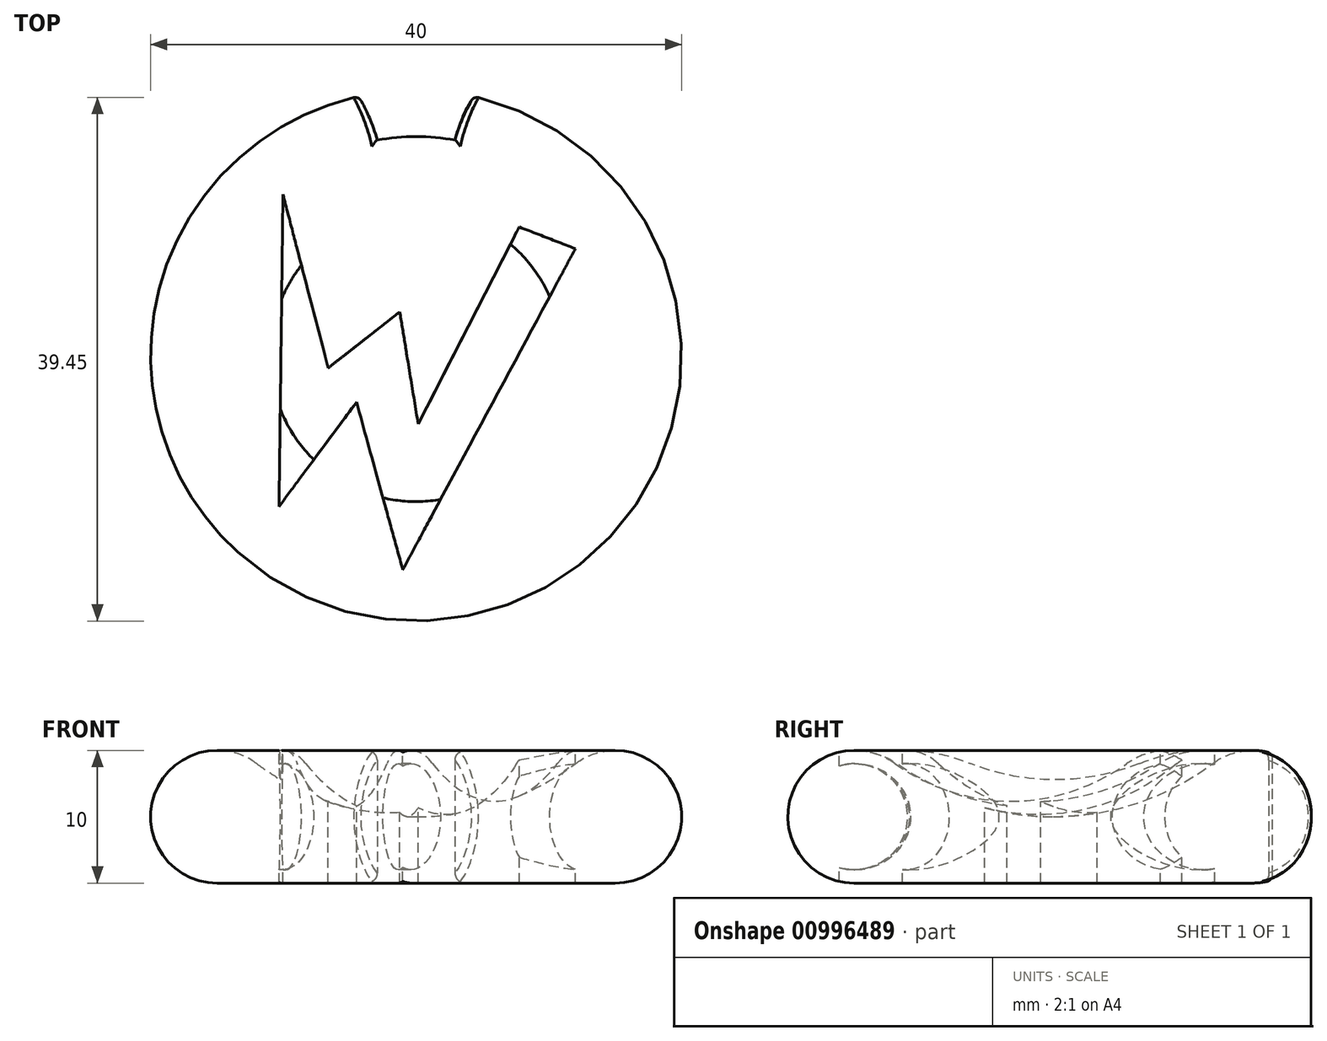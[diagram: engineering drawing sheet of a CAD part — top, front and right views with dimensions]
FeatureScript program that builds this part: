
annotation { "Feature Type Name" : "Feature", "Feature Type Description" : "" }
export const myFeature = defineFeature(function(context is Context, id is Id, definition is map)
    precondition{}
    {
        {
            var Q0;
            Q0=qCreatedBy(makeId("Front.planeOp"),FACE);
            var sketch = newSketch(context, id + "F0", { "sketchPlane" : qUnion([Q0])});
            skArc(sketch, "E0", {"start": v(-12, 9) * mm, "mid": v(-19.74, 6.58) * mm, "end": v(-15, 0) * mm});
            skArc(sketch, "E1", {"start": v(-12, 9) * mm, "mid": v(-6.32, 6.03) * mm, "end": v(0, 5) * mm});
            skLineSegment(sketch, "E2", {"start": v(-15, 0) * mm, "end": v(0, 0) * mm});
            skLineSegment(sketch, "E3", {"start": v(0, 0) * mm, "end": v(0, 5) * mm});
            skSolve(sketch);
        }
        {
            var Q0;
            Q0=makeQuery(id+"F0.imprint","IMPRINT",FACE,{"disambiguationData":[TD([[makeQuery(id+"F0.imprint","IMPRINT",EDGE,{"derivedFrom":sQuery(id+"F0.wireOp",EDGE,"E0")}),1.0]])]});
            var Q1;
            Q1=sQuery(id+"F0.wireOp",EDGE,"E3");
            revolve(context, id + "F1", {"surfaceOperationType" : NewSurfaceOperationType.NEW, "entities" : qUnion([Q0]), "axis" : qUnion([Q1]), "revolveType" : RevolveType.FULL});
        }
        {
            var Q0;
            Q0=qCreatedBy(makeId("Top.planeOp"),FACE);
            cPlane(context, id + "F2", {"entities" : qUnion([Q0]), "cplaneType" : CPlaneType.OFFSET, "offset" : 25 * mm, "width" : 150 * mm, "height" : 150 * mm});
        }
        {
            var Q0;
            Q0=qCreatedBy(id+"F2.planeOp",FACE);
            var sketch = newSketch(context, id + "F3", { "sketchPlane" : qUnion([Q0])});
            skLineSegment(sketch, "E4", {"start": v(-10.03, 12.15) * mm, "end": v(-10.33, -11.37) * mm});
            skLineSegment(sketch, "E5", {"start": v(-10.33, -11.37) * mm, "end": v(-4.49, -3.5) * mm});
            skLineSegment(sketch, "E6", {"start": v(-4.49, -3.5) * mm, "end": v(-1, -16.14) * mm});
            skLineSegment(sketch, "E7", {"start": v(-1, -16.14) * mm, "end": v(12, 8.06) * mm});
            skLineSegment(sketch, "E8", {"start": v(12, 8.06) * mm, "end": v(7.77, 9.7) * mm});
            skLineSegment(sketch, "E9", {"start": v(7.77, 9.7) * mm, "end": v(0.16, -5.16) * mm});
            skLineSegment(sketch, "E10", {"start": v(0.16, -5.16) * mm, "end": v(-1.23, 3.3) * mm});
            skLineSegment(sketch, "E11", {"start": v(-1.23, 3.3) * mm, "end": v(-6.63, -0.93) * mm});
            skLineSegment(sketch, "E12", {"start": v(-6.63, -0.93) * mm, "end": v(-10.03, 12.15) * mm});
            skSolve(sketch);
        }
        {
            var Q0;
            Q0 = qSketchRegion(id + "F3", true);
            extrude(context, id + "F4", {"entities" : qUnion([Q0]), "operationType" : NewBodyOperationType.REMOVE, "endBound" : BoundingType.THROUGH_ALL, "oppositeDirection" : true, "depth" : 21 * mm, "offsetDistance" : 25 * mm});
        }
        {
            var Q0;
            Q0=qCreatedBy(makeId("Front.planeOp"),FACE);
            var sketch = newSketch(context, id + "F5", { "sketchPlane" : qUnion([Q0])});
            skCircle(sketch, "E13", {"center": v(-15, 5) * mm, "radius": 4 * mm});
            skSolve(sketch);
        }
        {
            var Q0;
            Q0 = qSketchRegion(id + "F5", true);
            var Q1;
            Q1=sQuery(id+"F0.wireOp",EDGE,"E3");
            revolve(context, id + "F6", {"operationType" : NewBodyOperationType.ADD, "surfaceOperationType" : NewSurfaceOperationType.NEW, "entities" : qUnion([Q0]), "axis" : qUnion([Q1]), "revolveType" : RevolveType.FULL});
        }
        {
            var Q0;
            Q0=qCreatedBy(makeId("Top.planeOp"),FACE);
            var sketch = newSketch(context, id + "F7", { "sketchPlane" : qUnion([Q0])});
            skArc(sketch, "E14.MirrorC", {"start": v(2.93, 16.24) * mm, "mid": v(3.92, 18.78) * mm, "end": v(5.44, 21.05) * mm});
            skArc(sketch, "E15", {"start": v(2.93, 16.24) * mm, "mid": v(0, 16.5) * mm, "end": v(-2.93, 16.24) * mm});
            skArc(sketch, "E16", {"start": v(5.44, 21.05) * mm, "mid": v(0, 21.74) * mm, "end": v(-5.44, 21.05) * mm});
            skArc(sketch, "E17.trimOffspring", {"start": v(-2.93, 16.24) * mm, "mid": v(-3.92, 18.78) * mm, "end": v(-5.44, 21.05) * mm});
            skSolve(sketch);
        }
        {
            var Q0;
            Q0 = qSketchRegion(id + "F7", true);
            extrude(context, id + "F8", {"entities" : qUnion([Q0]), "operationType" : NewBodyOperationType.REMOVE, "depth" : 25 * mm, "offsetDistance" : 25 * mm});
        }
        {
            var Q0;
            Q0=makeQuery(id+"F8.boolean.opBoolean","INTERSECT",EDGE,{"derivedFrom":[makeQuery(id+"F1.opRevolve","SWEPT_FACE",FACE,{"disambiguationData":[OSD([sQuery(id+"F0.wireOp",EDGE,"E0")])]}),makeQuery(id+"F8.opExtrude","SWEPT_FACE",FACE,{"disambiguationData":[OSD([sQuery(id+"F7.wireOp",EDGE,"E17.trimOffspring")])]})]});
            var Q1;
            Q1=makeQuery(id+"F8.boolean.opBoolean","INTERSECT",EDGE,{"disambiguationData":[OD(0.0)],"derivedFrom":[makeQuery(id+"F1.opRevolve","SWEPT_FACE",FACE,{"disambiguationData":[OSD([sQuery(id+"F0.wireOp",EDGE,"E0")])]}),makeQuery(id+"F8.opExtrude","SWEPT_FACE",FACE,{"disambiguationData":[OSD([sQuery(id+"F7.wireOp",EDGE,"E15")])]})]});
            var Q2;
            Q2=makeQuery(id+"F8.boolean.opBoolean","INTERSECT",EDGE,{"disambiguationData":[OD(1.0)],"derivedFrom":[makeQuery(id+"F1.opRevolve","SWEPT_FACE",FACE,{"disambiguationData":[OSD([sQuery(id+"F0.wireOp",EDGE,"E0")])]}),makeQuery(id+"F8.opExtrude","SWEPT_FACE",FACE,{"disambiguationData":[OSD([sQuery(id+"F7.wireOp",EDGE,"E15")])]})]});
            var Q3;
            Q3=makeQuery(id+"F8.boolean.opBoolean","INTERSECT",EDGE,{"derivedFrom":[makeQuery(id+"F1.opRevolve","SWEPT_FACE",FACE,{"disambiguationData":[OSD([sQuery(id+"F0.wireOp",EDGE,"E0")])]}),makeQuery(id+"F8.opExtrude","SWEPT_FACE",FACE,{"disambiguationData":[OSD([sQuery(id+"F7.wireOp",EDGE,"E14.MirrorC")])]})]});
            fillet(context, id + "F9", {"entities" : qUnion([Q0, Q1, Q2, Q3]), "radius" : 0.5 * mm, "tangentPropagation" : true, "allowEdgeOverflow" : false});
        }
    });
